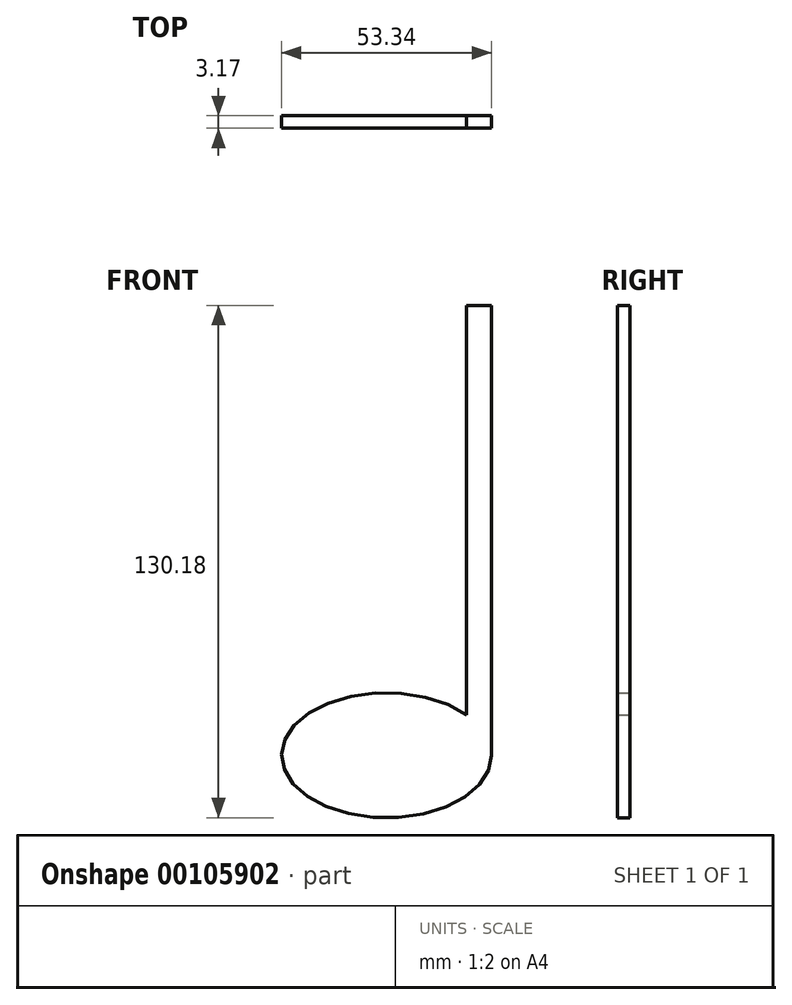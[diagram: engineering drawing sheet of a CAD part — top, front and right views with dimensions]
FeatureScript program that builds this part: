
annotation { "Feature Type Name" : "Feature", "Feature Type Description" : "" }
export const myFeature = defineFeature(function(context is Context, id is Id, definition is map)
    precondition{}
    {
        {
            var Q0;
            Q0=qCreatedBy(makeId("Front.planeOp"),FACE);
            var sketch = newSketch(context, id + "F0", { "sketchPlane" : qUnion([Q0])});
            skEllipticalArc(sketch, "E0", {});
            skLineSegment(sketch, "E1", {"start": v(26.67, 0) * mm, "end": v(26.67, 114.3) * mm});
            skPoint(sketch, "E1.endSnap0", {"position": v(26.67, 0) * mm});
            skLineSegment(sketch, "E2", {"start": v(26.67, 114.3) * mm, "end": v(20.32, 114.3) * mm});
            skLineSegment(sketch, "E3", {"start": v(20.32, 114.3) * mm, "end": v(20.32, 10.28) * mm});
            const initialGuessF0  = {"E0": [0, 0, 1, 0, 0.02667, 0.015875, 0.7045474184528451, 0]};
            skSetInitialGuess(sketch, initialGuessF0);
            skSolve(sketch);
        }
        {
            var Q0;
            Q0=qSketchRegion(id+"F0",true);
            extrude(context, id + "F1", {"entities" : qUnion([Q0]), "depth" : 3.17 * mm});
        }
    });
